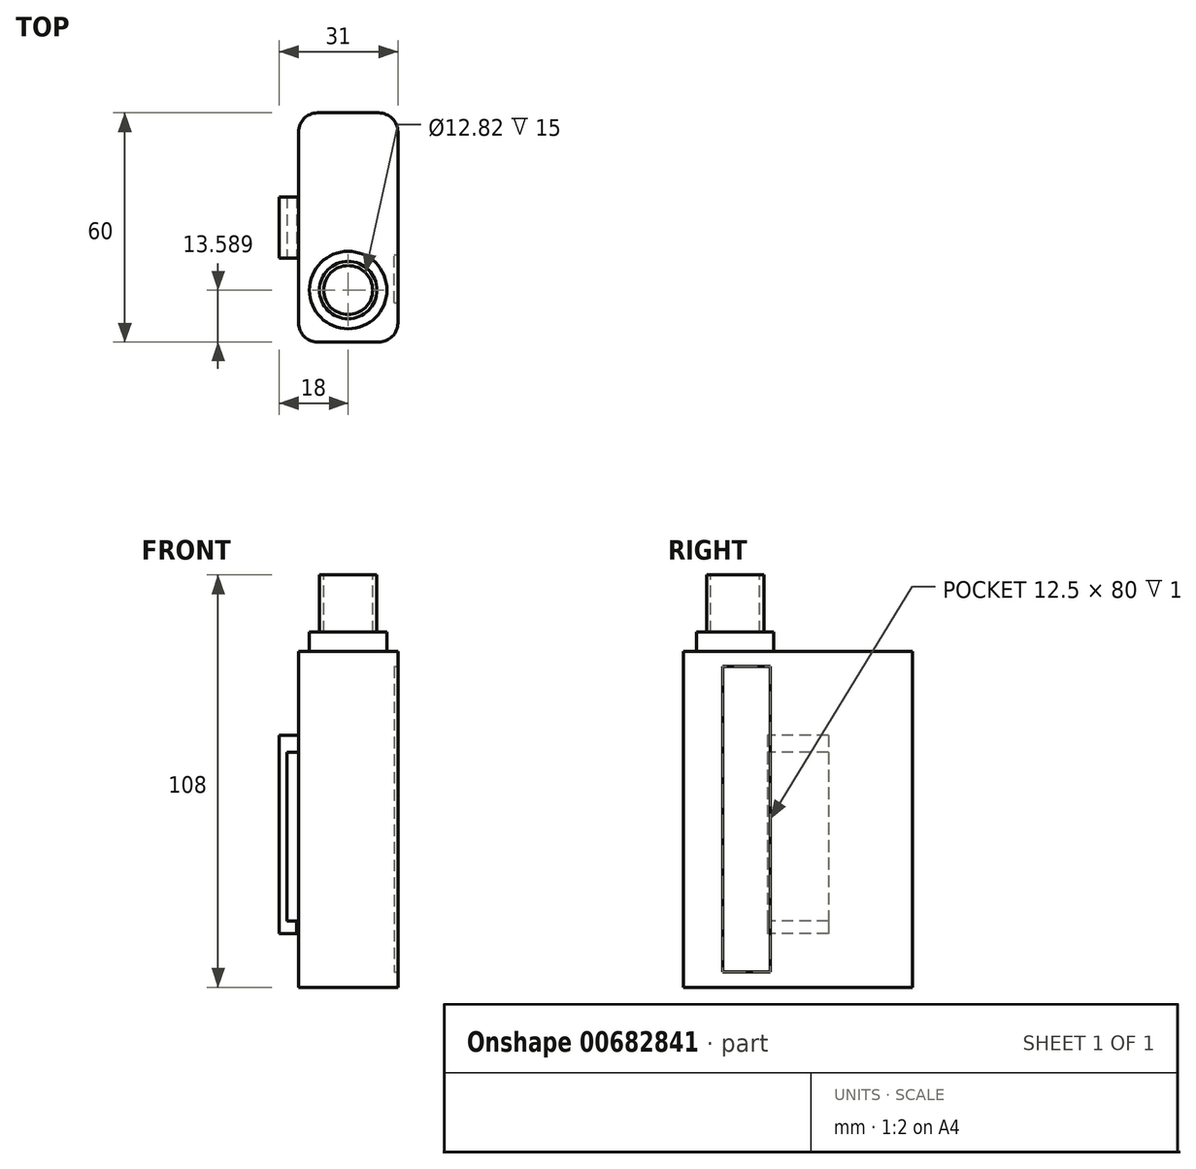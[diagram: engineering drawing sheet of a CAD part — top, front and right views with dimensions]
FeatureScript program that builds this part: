
annotation { "Feature Type Name" : "Feature", "Feature Type Description" : "" }
export const myFeature = defineFeature(function(context is Context, id is Id, definition is map)
    precondition{}
    {
        {
            var Q0;
            Q0=qCreatedBy(makeId("Front.planeOp"),FACE);
            var sketch = newSketch(context, id + "F0", { "sketchPlane" : qUnion([Q0])});
            skLineSegment(sketch, "E0.bottom", {"start": v(-13, 44) * mm, "end": v(13, 44) * mm});
            skLineSegment(sketch, "E0.top", {"start": v(-13, -44) * mm, "end": v(13, -44) * mm});
            skLineSegment(sketch, "E0.left", {"start": v(-13, 44) * mm, "end": v(-13, -44) * mm});
            skLineSegment(sketch, "E0.right", {"start": v(13, 44) * mm, "end": v(13, -44) * mm});
            skSolve(sketch);
        }
        {
            var Q0;
            Q0=makeQuery(id+"F0.imprint","IMPRINT",FACE,{"disambiguationData":[TD([[makeQuery(id+"F0.imprint","IMPRINT",EDGE,{"derivedFrom":sQuery(id+"F0.wireOp",EDGE,"E0.bottom")}),-1.0]])]});
            extrude(context, id + "F1", {"entities" : qUnion([Q0]), "depth" : 30 * mm, "offsetDistance" : 25 * mm});
        }
        {
            var Q0;
            Q0=makeQuery(id+"F1.opExtrude","CAP_FACE",FACE,{"disambiguationData":[OSD([sQuery(id+"F0.wireOp",EDGE,"E0.bottom"),sQuery(id+"F0.wireOp",EDGE,"E0.top"),sQuery(id+"F0.wireOp",EDGE,"E0.left"),sQuery(id+"F0.wireOp",EDGE,"E0.right")])],"isStart":true});
            extrude(context, id + "F2", {"entities" : qUnion([Q0]), "operationType" : NewBodyOperationType.ADD, "depth" : 30 * mm, "offsetDistance" : 25 * mm});
        }
        {
            var Q0;
            Q0=makeQuery(id+"F2.opExtrude","CAP_EDGE",EDGE,{"disambiguationData":[OSD([sQuery(id+"F0.wireOp",EDGE,"E0.right")])],"isStart":false});
            var Q1;
            Q1=makeQuery(id+"F2.opExtrude","CAP_EDGE",EDGE,{"disambiguationData":[OSD([sQuery(id+"F0.wireOp",EDGE,"E0.left")])],"isStart":false});
            var Q2;
            Q2=makeQuery(id+"F1.opExtrude","CAP_EDGE",EDGE,{"disambiguationData":[OSD([sQuery(id+"F0.wireOp",EDGE,"E0.left")])],"isStart":false});
            var Q3;
            Q3=makeQuery(id+"F1.opExtrude","CAP_EDGE",EDGE,{"disambiguationData":[OSD([sQuery(id+"F0.wireOp",EDGE,"E0.right")])],"isStart":false});
            fillet(context, id + "F3", {"entities" : qUnion([Q0, Q1, Q2, Q3]), "radius" : 5 * mm, "tangentPropagation" : true, "allowEdgeOverflow" : false});
        }
        {
            var Q0;
            {var subQ0=sQuery(id+"F0.wireOp",EDGE,"E0.bottom");Q0=makeQuery(id+"F2.boolean.opBoolean","MERGE",FACE,{"derivedFrom":[makeQuery(id+"F1.opExtrude","SWEPT_FACE",FACE,{"disambiguationData":[OSD([subQ0])]}),makeQuery(id+"F2.opExtrude","SWEPT_FACE",FACE,{"disambiguationData":[OSD([subQ0])]})]});}
            var sketch = newSketch(context, id + "F4", { "sketchPlane" : qUnion([Q0])});
            skCircle(sketch, "E1", {"center": v(0, -16.41) * mm, "radius": 10.15 * mm});
            skSolve(sketch);
        }
        {
            var Q0;
            Q0=makeQuery(id+"F4.imprint","IMPRINT",FACE,{"disambiguationData":[TD([[makeQuery(id+"F4.imprint","IMPRINT",EDGE,{"derivedFrom":sQuery(id+"F4.wireOp",EDGE,"E1")}),1.0]])]});
            extrude(context, id + "F5", {"entities" : qUnion([Q0]), "operationType" : NewBodyOperationType.ADD, "depth" : 5 * mm, "offsetDistance" : 25 * mm});
        }
        {
            var Q0;
            Q0=makeQuery(id+"F5.opExtrude","CAP_FACE",FACE,{"disambiguationData":[OSD([sQuery(id+"F4.wireOp",EDGE,"E1")])],"isStart":false});
            var sketch = newSketch(context, id + "F6", { "sketchPlane" : qUnion([Q0])});
            skCircle(sketch, "E2", {"center": v(0, -16.41) * mm, "radius": 7.5 * mm});
            skSolve(sketch);
        }
        {
            var Q0;
            Q0=makeQuery(id+"F6.imprint","IMPRINT",FACE,{"disambiguationData":[TD([[makeQuery(id+"F6.imprint","IMPRINT",EDGE,{"derivedFrom":sQuery(id+"F6.wireOp",EDGE,"E2")}),1.0]])]});
            extrude(context, id + "F7", {"entities" : qUnion([Q0]), "operationType" : NewBodyOperationType.ADD, "depth" : 15 * mm, "offsetDistance" : 25 * mm});
        }
        {
            var Q0;
            Q0=makeQuery(id+"F7.opExtrude","CAP_FACE",FACE,{"disambiguationData":[OSD([sQuery(id+"F6.wireOp",EDGE,"E2")])],"isStart":false});
            var sketch = newSketch(context, id + "F8", { "sketchPlane" : qUnion([Q0])});
            skCircle(sketch, "E3", {"center": v(0, -16.41) * mm, "radius": 6.41 * mm});
            skSolve(sketch);
        }
        {
            var Q0;
            Q0 = qSketchRegion(id + "F8", true);
            extrude(context, id + "F9", {"entities" : qUnion([Q0]), "operationType" : NewBodyOperationType.REMOVE, "oppositeDirection" : true, "depth" : 15 * mm, "offsetDistance" : 25 * mm});
        }
        {
            var Q0;
            {var subQ0=sQuery(id+"F0.wireOp",EDGE,"E0.right");Q0=makeQuery(id+"F2.boolean.opBoolean","MERGE",FACE,{"derivedFrom":[makeQuery(id+"F1.opExtrude","SWEPT_FACE",FACE,{"disambiguationData":[OSD([subQ0])]}),makeQuery(id+"F2.opExtrude","SWEPT_FACE",FACE,{"disambiguationData":[OSD([subQ0])]})]});}
            var sketch = newSketch(context, id + "F10", { "sketchPlane" : qUnion([Q0])});
            skLineSegment(sketch, "E4.bottom", {"start": v(-19.7, 40) * mm, "end": v(-7.2, 40) * mm});
            skLineSegment(sketch, "E4.top", {"start": v(-19.7, -40) * mm, "end": v(-7.2, -40) * mm});
            skLineSegment(sketch, "E4.left", {"start": v(-19.7, 40) * mm, "end": v(-19.7, -40) * mm});
            skLineSegment(sketch, "E4.right", {"start": v(-7.2, 40) * mm, "end": v(-7.2, -40) * mm});
            skSolve(sketch);
        }
        {
            var Q0;
            Q0=makeQuery(id+"F10.imprint","IMPRINT",FACE,{"disambiguationData":[TD([[makeQuery(id+"F10.imprint","IMPRINT",EDGE,{"derivedFrom":sQuery(id+"F10.wireOp",EDGE,"E4.bottom")}),-1.0]])]});
            extrude(context, id + "F11", {"entities" : qUnion([Q0]), "operationType" : NewBodyOperationType.REMOVE, "oppositeDirection" : true, "depth" : 1 * mm, "offsetDistance" : 25 * mm});
        }
        {
            var Q0;
            {var subQ0=sQuery(id+"F0.wireOp",EDGE,"E0.left");Q0=makeQuery(id+"F2.boolean.opBoolean","MERGE",FACE,{"derivedFrom":[makeQuery(id+"F1.opExtrude","SWEPT_FACE",FACE,{"disambiguationData":[OSD([subQ0])]}),makeQuery(id+"F2.opExtrude","SWEPT_FACE",FACE,{"disambiguationData":[OSD([subQ0])]})]});}
            var sketch = newSketch(context, id + "F12", { "sketchPlane" : qUnion([Q0])});
            skLineSegment(sketch, "E5.bottom", {"start": v(-8, 22) * mm, "end": v(8, 22) * mm});
            skLineSegment(sketch, "E5.top", {"start": v(-8, -30) * mm, "end": v(8, -30) * mm});
            skLineSegment(sketch, "E5.left", {"start": v(-8, 22) * mm, "end": v(-8, -30) * mm});
            skLineSegment(sketch, "E5.right", {"start": v(8, 22) * mm, "end": v(8, -30) * mm});
            skSolve(sketch);
        }
        {
            var Q0;
            Q0=makeQuery(id+"F12.imprint","IMPRINT",FACE,{"disambiguationData":[TD([[makeQuery(id+"F12.imprint","IMPRINT",EDGE,{"derivedFrom":sQuery(id+"F12.wireOp",EDGE,"E5.bottom")}),-1.0]])]});
            extrude(context, id + "F13", {"entities" : qUnion([Q0]), "operationType" : NewBodyOperationType.ADD, "depth" : 5 * mm, "offsetDistance" : 25 * mm});
        }
        {
            var Q0;
            Q0=makeQuery(id+"F13.opExtrude","SWEPT_FACE",FACE,{"disambiguationData":[OSD([sQuery(id+"F12.wireOp",EDGE,"E5.right")])]});
            var sketch = newSketch(context, id + "F14", { "sketchPlane" : qUnion([Q0])});
            skLineSegment(sketch, "E6.bottom", {"start": v(-13, 17.55) * mm, "end": v(-16, 17.55) * mm});
            skLineSegment(sketch, "E6.top", {"start": v(-13, -26.7) * mm, "end": v(-16, -26.7) * mm});
            skLineSegment(sketch, "E6.left", {"start": v(-13, 17.55) * mm, "end": v(-13, -26.7) * mm});
            skLineSegment(sketch, "E6.right", {"start": v(-16, 17.55) * mm, "end": v(-16, -26.7) * mm});
            skSolve(sketch);
        }
        {
            var Q0;
            Q0=makeQuery(id+"F14.imprint","IMPRINT",FACE,{"disambiguationData":[TD([[makeQuery(id+"F14.imprint","IMPRINT",EDGE,{"derivedFrom":sQuery(id+"F14.wireOp",EDGE,"E6.bottom")}),1.0]])]});
            extrude(context, id + "F15", {"entities" : qUnion([Q0]), "operationType" : NewBodyOperationType.REMOVE, "oppositeDirection" : true, "depth" : 16 * mm, "offsetDistance" : 25 * mm});
        }
        {
            var Q0;
            Q0=makeQuery(id+"F13.opExtrude","SWEPT_FACE",FACE,{"disambiguationData":[OSD([sQuery(id+"F12.wireOp",EDGE,"E5.right")])]});
            var sketch = newSketch(context, id + "F16", { "sketchPlane" : qUnion([Q0])});
            skLineSegment(sketch, "E7.bottom", {"start": v(-13, -26.7) * mm, "end": v(-13.5, -26.7) * mm});
            skLineSegment(sketch, "E7.top", {"start": v(-13, -30) * mm, "end": v(-13.5, -30) * mm});
            skLineSegment(sketch, "E7.left", {"start": v(-13, -26.7) * mm, "end": v(-13, -30) * mm});
            skLineSegment(sketch, "E7.right", {"start": v(-13.5, -26.7) * mm, "end": v(-13.5, -30) * mm});
            skSolve(sketch);
        }
        {
            var Q0;
            Q0 = qSketchRegion(id + "F16", true);
            extrude(context, id + "F17", {"entities" : qUnion([Q0]), "operationType" : NewBodyOperationType.REMOVE, "oppositeDirection" : true, "depth" : 16 * mm, "offsetDistance" : 25 * mm});
        }
    });
